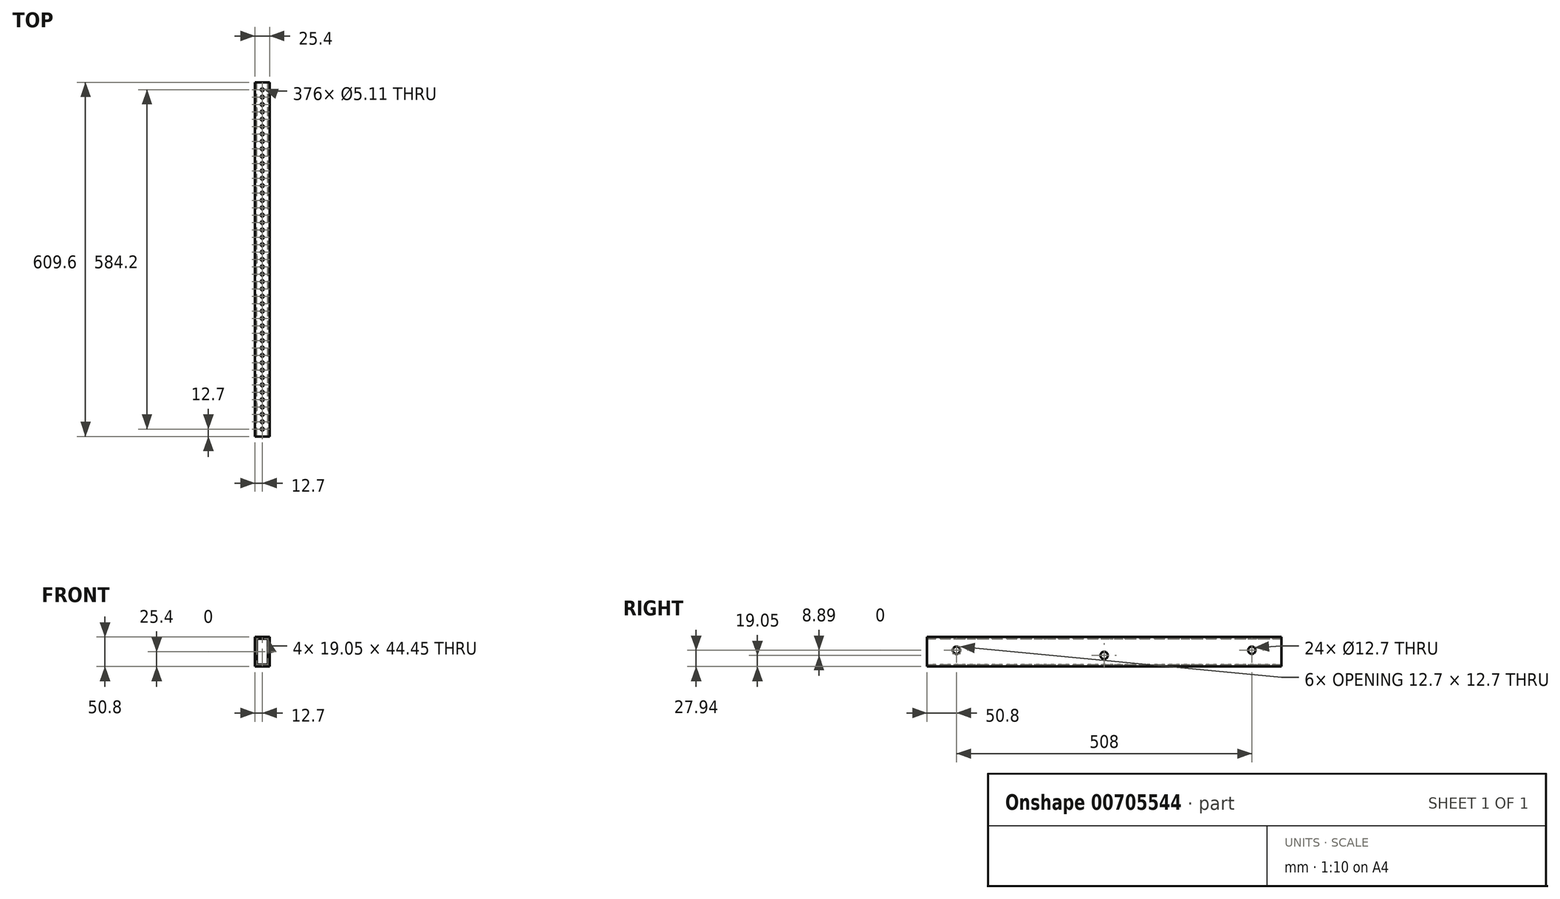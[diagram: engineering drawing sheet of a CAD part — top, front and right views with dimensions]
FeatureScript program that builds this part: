
annotation { "Feature Type Name" : "Feature", "Feature Type Description" : "" }
export const myFeature = defineFeature(function(context is Context, id is Id, definition is map)
    precondition{}
    {
        {
            var Q0;
            Q0=qCreatedBy(makeId("Front.planeOp"),FACE);
            var sketch = newSketch(context, id + "F0", { "sketchPlane" : qUnion([Q0])});
            skLineSegment(sketch, "E0.bottom", {"start": v(0, 0) * mm, "end": v(25.4, 0) * mm});
            skLineSegment(sketch, "E0.top", {"start": v(0, 50.8) * mm, "end": v(25.4, 50.8) * mm});
            skLineSegment(sketch, "E0.left", {"start": v(0, 0) * mm, "end": v(0, 50.8) * mm});
            skLineSegment(sketch, "E0.right", {"start": v(25.4, 0) * mm, "end": v(25.4, 50.8) * mm});
            skLineSegment(sketch, "E1.0", {"start": v(3.17, 47.63) * mm, "end": v(22.22, 47.63) * mm});
            skLineSegment(sketch, "E1.1", {"start": v(3.17, 3.17) * mm, "end": v(3.17, 47.63) * mm});
            skLineSegment(sketch, "E1.2", {"start": v(3.17, 3.17) * mm, "end": v(22.22, 3.17) * mm});
            skLineSegment(sketch, "E1.3", {"start": v(22.22, 3.17) * mm, "end": v(22.22, 47.63) * mm});
            skSolve(sketch);
        }
        {
            var Q0;
            Q0=makeQuery(id+"F0.imprint","IMPRINT",FACE,{"disambiguationData":[TD([[makeQuery(id+"F0.imprint","IMPRINT",EDGE,{"derivedFrom":sQuery(id+"F0.wireOp",EDGE,"E0.bottom")}),1.0]])]});
            extrude(context, id + "F1", {"entities" : qUnion([Q0]), "endBound" : BoundingType.SYMMETRIC, "depth" : 609.6 * mm, "offsetDistance" : 25.4 * mm});
        }
        {
            var Q0;
            Q0=makeQuery(id+"F1.opExtrude","SWEPT_FACE",FACE,{"disambiguationData":[OSD([sQuery(id+"F0.wireOp",EDGE,"E0.top")])]});
            var sketch = newSketch(context, id + "F2", { "sketchPlane" : qUnion([Q0])});
            skLineSegment(sketch, "E2", {"start": v(12.7, 304.8) * mm, "end": v(12.7, 292.1) * mm});
            skCircle(sketch, "E3", {"center": v(12.7, 292.1) * mm, "radius": 2.55 * mm});
            skCircle(sketch, "E4.0.1.0", {"center": v(12.7, 279.4) * mm, "radius": 2.55 * mm});
            skCircle(sketch, "E4.0.2.0", {"center": v(12.7, 266.7) * mm, "radius": 2.55 * mm});
            skCircle(sketch, "E4.0.3.0", {"center": v(12.7, 254) * mm, "radius": 2.55 * mm});
            skCircle(sketch, "E4.0.4.0", {"center": v(12.7, 241.3) * mm, "radius": 2.55 * mm});
            skCircle(sketch, "E4.0.5.0", {"center": v(12.7, 228.6) * mm, "radius": 2.55 * mm});
            skCircle(sketch, "E4.0.6.0", {"center": v(12.7, 215.9) * mm, "radius": 2.55 * mm});
            skCircle(sketch, "E4.0.7.0", {"center": v(12.7, 203.2) * mm, "radius": 2.55 * mm});
            skCircle(sketch, "E4.0.8.0", {"center": v(12.7, 190.5) * mm, "radius": 2.55 * mm});
            skCircle(sketch, "E4.0.9.0", {"center": v(12.7, 177.8) * mm, "radius": 2.55 * mm});
            skCircle(sketch, "E4.0.10.0", {"center": v(12.7, 165.1) * mm, "radius": 2.55 * mm});
            skCircle(sketch, "E4.0.11.0", {"center": v(12.7, 152.4) * mm, "radius": 2.55 * mm});
            skCircle(sketch, "E4.0.12.0", {"center": v(12.7, 139.7) * mm, "radius": 2.55 * mm});
            skCircle(sketch, "E4.0.13.0", {"center": v(12.7, 127) * mm, "radius": 2.55 * mm});
            skCircle(sketch, "E4.0.14.0", {"center": v(12.7, 114.3) * mm, "radius": 2.55 * mm});
            skCircle(sketch, "E4.0.15.0", {"center": v(12.7, 101.6) * mm, "radius": 2.55 * mm});
            skCircle(sketch, "E4.0.16.0", {"center": v(12.7, 88.9) * mm, "radius": 2.55 * mm});
            skCircle(sketch, "E4.0.17.0", {"center": v(12.7, 76.2) * mm, "radius": 2.55 * mm});
            skCircle(sketch, "E4.0.18.0", {"center": v(12.7, 63.5) * mm, "radius": 2.55 * mm});
            skCircle(sketch, "E4.0.19.0", {"center": v(12.7, 50.8) * mm, "radius": 2.55 * mm});
            skCircle(sketch, "E4.0.20.0", {"center": v(12.7, 38.1) * mm, "radius": 2.55 * mm});
            skCircle(sketch, "E4.0.21.0", {"center": v(12.7, 25.4) * mm, "radius": 2.55 * mm});
            skCircle(sketch, "E4.0.22.0", {"center": v(12.7, 12.7) * mm, "radius": 2.55 * mm});
            skCircle(sketch, "E4.0.23.0", {"center": v(12.7, 0) * mm, "radius": 2.55 * mm});
            skCircle(sketch, "E4.0.24.0", {"center": v(12.7, -12.7) * mm, "radius": 2.55 * mm});
            skCircle(sketch, "E4.0.25.0", {"center": v(12.7, -25.4) * mm, "radius": 2.55 * mm});
            skCircle(sketch, "E4.0.26.0", {"center": v(12.7, -38.1) * mm, "radius": 2.55 * mm});
            skCircle(sketch, "E4.0.27.0", {"center": v(12.7, -50.8) * mm, "radius": 2.55 * mm});
            skCircle(sketch, "E4.0.28.0", {"center": v(12.7, -63.5) * mm, "radius": 2.55 * mm});
            skCircle(sketch, "E4.0.29.0", {"center": v(12.7, -76.2) * mm, "radius": 2.55 * mm});
            skCircle(sketch, "E4.0.30.0", {"center": v(12.7, -88.9) * mm, "radius": 2.55 * mm});
            skCircle(sketch, "E4.0.31.0", {"center": v(12.7, -101.6) * mm, "radius": 2.55 * mm});
            skCircle(sketch, "E4.0.32.0", {"center": v(12.7, -114.3) * mm, "radius": 2.55 * mm});
            skCircle(sketch, "E4.0.33.0", {"center": v(12.7, -127) * mm, "radius": 2.55 * mm});
            skCircle(sketch, "E4.0.34.0", {"center": v(12.7, -139.7) * mm, "radius": 2.55 * mm});
            skCircle(sketch, "E4.0.35.0", {"center": v(12.7, -152.4) * mm, "radius": 2.55 * mm});
            skCircle(sketch, "E4.0.36.0", {"center": v(12.7, -165.1) * mm, "radius": 2.55 * mm});
            skCircle(sketch, "E4.0.37.0", {"center": v(12.7, -177.8) * mm, "radius": 2.55 * mm});
            skCircle(sketch, "E4.0.38.0", {"center": v(12.7, -190.5) * mm, "radius": 2.55 * mm});
            skCircle(sketch, "E4.0.39.0", {"center": v(12.7, -203.2) * mm, "radius": 2.55 * mm});
            skCircle(sketch, "E4.0.40.0", {"center": v(12.7, -215.9) * mm, "radius": 2.55 * mm});
            skCircle(sketch, "E4.0.41.0", {"center": v(12.7, -228.6) * mm, "radius": 2.55 * mm});
            skCircle(sketch, "E4.0.42.0", {"center": v(12.7, -241.3) * mm, "radius": 2.55 * mm});
            skCircle(sketch, "E4.0.43.0", {"center": v(12.7, -254) * mm, "radius": 2.55 * mm});
            skCircle(sketch, "E4.0.44.0", {"center": v(12.7, -266.7) * mm, "radius": 2.55 * mm});
            skCircle(sketch, "E4.0.45.0", {"center": v(12.7, -279.4) * mm, "radius": 2.55 * mm});
            skCircle(sketch, "E4.0.46.0", {"center": v(12.7, -292.1) * mm, "radius": 2.55 * mm});
            skLineSegment(sketch, "E4.direction1", {"start": v(12.7, 292.1) * mm, "end": v(12.7, 292.1) * mm});
            skLineSegment(sketch, "E4.direction2", {"start": v(12.7, 292.1) * mm, "end": v(12.7, 279.4) * mm, "construction": true});
            skSolve(sketch);
        }
        {
            var Q0;
            Q0 = qSketchRegion(id + "F2", true);
            extrude(context, id + "F3", {"entities" : qUnion([Q0]), "operationType" : NewBodyOperationType.REMOVE, "endBound" : BoundingType.THROUGH_ALL, "oppositeDirection" : true, "depth" : 25.4 * mm, "offsetDistance" : 25.4 * mm});
        }
        {
            var Q0;
            Q0=makeQuery(id+"F1.opExtrude","SWEPT_FACE",FACE,{"disambiguationData":[OSD([sQuery(id+"F0.wireOp",EDGE,"E0.right")])]});
            var sketch = newSketch(context, id + "F4", { "sketchPlane" : qUnion([Q0])});
            skLineSegment(sketch, "E5", {"start": v(0, 19.05) * mm, "end": v(0, 27.94) * mm});
            skCircle(sketch, "E6", {"center": v(0, 19.05) * mm, "radius": 6.35 * mm});
            skCircle(sketch, "E7", {"center": v(-254, 27.94) * mm, "radius": 6.35 * mm});
            skCircle(sketch, "E8", {"center": v(254, 27.94) * mm, "radius": 6.35 * mm});
            skLineSegment(sketch, "E9", {"start": v(-254, 27.94) * mm, "end": v(0, 19.05) * mm});
            skLineSegment(sketch, "E10", {"start": v(0, 19.05) * mm, "end": v(254, 27.94) * mm});
            skSolve(sketch);
        }
        {
            var Q0;
            Q0=makeQuery(id+"F4.imprint","IMPRINT",FACE,{"disambiguationData":[TD([[makeQuery(id+"F4.imprint","IMPRINT",EDGE,{"derivedFrom":sQuery(id+"F4.wireOp",EDGE,"E7")}),1.0]])]});
            var Q1;
            {var subQ0=sQuery(id+"F4.wireOp",EDGE,"E10");var subQ1=sQuery(id+"F4.wireOp",EDGE,"E6");var subQ2=makeQuery(id+"F4.imprint","INTERSECT",VERTEX,{"derivedFrom":[subQ1,subQ0]});Q1=makeQuery(id+"F4.imprint","IMPRINT",FACE,{"disambiguationData":[TD([[makeQuery(id+"F4.imprint","IMPRINT",EDGE,{"disambiguationData":[TD([[subQ2,1.0]])],"derivedFrom":subQ1}),1.0]])]});}
            var Q2;
            {var subQ1=sQuery(id+"F4.wireOp",EDGE,"E5");var subQ3=sQuery(id+"F4.wireOp",EDGE,"E6");var subQ4=makeQuery(id+"F4.imprint","INTERSECT",VERTEX,{"derivedFrom":[subQ1,subQ3]});Q2=makeQuery(id+"F4.imprint","IMPRINT",FACE,{"disambiguationData":[TD([[makeQuery(id+"F4.imprint","IMPRINT",EDGE,{"disambiguationData":[TD([[subQ4,1.0]])],"derivedFrom":subQ3}),1.0]])]});}
            var Q3;
            {var subQ1=sQuery(id+"F4.wireOp",EDGE,"E5");var subQ3=sQuery(id+"F4.wireOp",EDGE,"E6");var subQ4=makeQuery(id+"F4.imprint","INTERSECT",VERTEX,{"derivedFrom":[subQ1,subQ3]});Q3=makeQuery(id+"F4.imprint","IMPRINT",FACE,{"disambiguationData":[TD([[makeQuery(id+"F4.imprint","IMPRINT",EDGE,{"disambiguationData":[TD([[subQ4,-1.0]])],"derivedFrom":subQ3}),1.0]])]});}
            var Q4;
            Q4=makeQuery(id+"F4.imprint","IMPRINT",FACE,{"disambiguationData":[TD([[makeQuery(id+"F4.imprint","IMPRINT",EDGE,{"derivedFrom":sQuery(id+"F4.wireOp",EDGE,"E8")}),1.0]])]});
            extrude(context, id + "F5", {"entities" : qUnion([Q0, Q1, Q2, Q3, Q4]), "operationType" : NewBodyOperationType.REMOVE, "endBound" : BoundingType.THROUGH_ALL, "oppositeDirection" : true, "depth" : 25.4 * mm, "offsetDistance" : 25.4 * mm});
        }
    });
